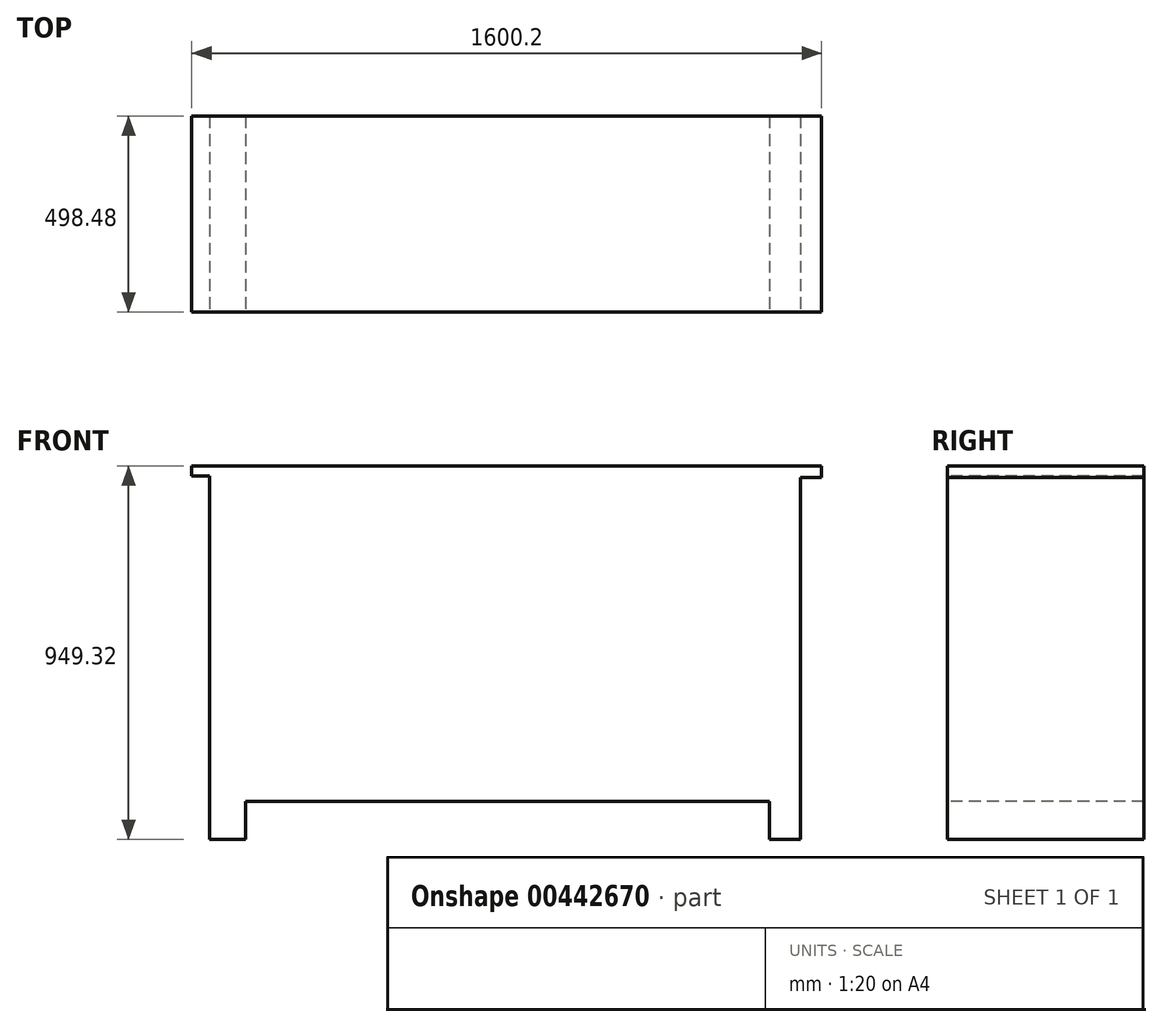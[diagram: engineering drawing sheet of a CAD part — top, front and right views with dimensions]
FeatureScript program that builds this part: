
annotation { "Feature Type Name" : "Feature", "Feature Type Description" : "" }
export const myFeature = defineFeature(function(context is Context, id is Id, definition is map)
    precondition{}
    {
        {
            var Q0;
            Q0=qCreatedBy(makeId("Front.planeOp"),FACE);
            var sketch = newSketch(context, id + "F0", { "sketchPlane" : qUnion([Q0])});
            skLineSegment(sketch, "E0.bottom", {"start": v(0, 0) * mm, "end": v(1600.2, 0) * mm});
            skLineSegment(sketch, "E0.top", {"start": v(0, 949.33) * mm, "end": v(1600.2, 949.33) * mm});
            skLineSegment(sketch, "E0.left", {"start": v(0, 0) * mm, "end": v(0, 949.33) * mm});
            skLineSegment(sketch, "E0.right", {"start": v(1600.2, 0) * mm, "end": v(1600.2, 949.33) * mm});
            skSolve(sketch);
        }
        {
            var Q0;
            Q0=makeQuery(id+"F0.imprint","IMPRINT",FACE,{"disambiguationData":[TD([[makeQuery(id+"F0.imprint","IMPRINT",EDGE,{"derivedFrom":sQuery(id+"F0.wireOp",EDGE,"E0.bottom")}),1.0]])]});
            extrude(context, id + "F1", {"entities" : qUnion([Q0]), "depth" : 498.47 * mm});
        }
        {
            var Q0;
            Q0=makeQuery(id+"F1.opExtrude","CAP_FACE",FACE,{"disambiguationData":[OSD([sQuery(id+"F0.wireOp",EDGE,"E0.bottom"),sQuery(id+"F0.wireOp",EDGE,"E0.top"),sQuery(id+"F0.wireOp",EDGE,"E0.left"),sQuery(id+"F0.wireOp",EDGE,"E0.right")])],"isStart":false});
            var sketch = newSketch(context, id + "F2", { "sketchPlane" : qUnion([Q0])});
            skLineSegment(sketch, "E1.bottom", {"start": v(0, 0) * mm, "end": v(45.16, 0) * mm});
            skLineSegment(sketch, "E1.top", {"start": v(0, 923.2) * mm, "end": v(45.16, 923.2) * mm});
            skLineSegment(sketch, "E1.left", {"start": v(0, 0) * mm, "end": v(0, 923.2) * mm});
            skLineSegment(sketch, "E1.right", {"start": v(45.16, 0) * mm, "end": v(45.16, 923.2) * mm});
            skLineSegment(sketch, "E2.bottom", {"start": v(1600.2, 0) * mm, "end": v(1547.06, 0) * mm});
            skLineSegment(sketch, "E2.top", {"start": v(1600.2, 919) * mm, "end": v(1547.06, 919) * mm});
            skLineSegment(sketch, "E2.left", {"start": v(1600.2, 0) * mm, "end": v(1600.2, 919) * mm});
            skLineSegment(sketch, "E2.right", {"start": v(1547.06, 0) * mm, "end": v(1547.06, 919) * mm});
            skLineSegment(sketch, "E3.bottom", {"start": v(137.2, 0) * mm, "end": v(1467.58, 0) * mm});
            skLineSegment(sketch, "E3.top", {"start": v(137.2, 96.93) * mm, "end": v(1467.58, 96.93) * mm});
            skLineSegment(sketch, "E3.left", {"start": v(137.2, 0) * mm, "end": v(137.2, 96.93) * mm});
            skLineSegment(sketch, "E3.right", {"start": v(1467.58, 0) * mm, "end": v(1467.58, 96.93) * mm});
            skSolve(sketch);
        }
        {
            var Q0;
            Q0 = qSketchRegion(id + "F2", true);
            extrude(context, id + "F3", {"entities" : qUnion([Q0]), "operationType" : NewBodyOperationType.REMOVE, "oppositeDirection" : true, "depth" : 508 * mm});
        }
    });
